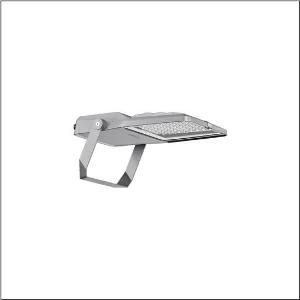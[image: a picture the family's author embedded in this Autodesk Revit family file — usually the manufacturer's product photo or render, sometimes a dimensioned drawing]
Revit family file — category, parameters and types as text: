
# Revit family: floodlight_fl_21_mini___pl33t_5xa7776b2f1a_8d7b
name_source: partatom
category: Lighting Fixtures
units: mm (PartAtom-declared; Revit-internal decimal feet)

## family parameters
Cut with Voids When Loaded = No
Host = Face
Light Source = No
Part Type = Normal
Room Calculation Point = No
Round Connector Dimension = Use Diameter
Shared = No

## types (1)
- --- (1 x LED, 6150 lm, 45.7 W, 3000K)
    Apparent Load = 46 VA
    CIE Flux Codes = 26 75 99 100 100
    Color Rendering = 70
    Color Temperature = 3000K
    Default Elevation = 1800 mm
    Description = Floodlight FL 21 mini, floodlight, primary light control with lens, of PMMA, primary optical cover: protective disc, of toughened safety glass, transparent, light distribution: PL33T, light emission: direct distribution, installation type: surface-mounted, LED, High Power LED, rated luminous flux: 6.150lm, luminous efficacy: 135lm/W, light colour: 730, colour temperature: 3000K, control: flexible luminous flux parameterisation, time-dependent luminous flux control, constant luminous flux control, overheat protection, presetting dimming logarithmic, with terminal, 6-pole, mains connection: 220..240V, AC, 50/60Hz, start of lifetime: 46W, end of service life: 48W, reduction: 22W, luminaire housing, of diecast aluminium, powder-coated, Siteco® metallic grey (DB 702S), corrosivity category C5 mid according to DIN EN ISO 12944, sealing non-destructively replaceable, mounting bracket, of steel, galvanised, powder-coated, Siteco® metallic grey (DB 702S), Smart Interface below and above, protection rating (complete): IP66, insulation class (complete): insulation class II (safety insulation), certification: CE, ENEC, VDE, protection symbol: D, impact resistance: IK08, permissible operating ambient temperature: -40..+40°C, permissible operating ambient temperature for outdoor applications: -40..+50°C, standard: DIN EN 12944, LABS conformity tested according to VDMA 24364:2018-05, packaging unit: 1 piece

Light Distribution: PL33T
    Height = 70 mm
    Lamp = 1 x LED
    Lamp Light Flux = 6150 lm
    Lamp Power = 45.7 W
    Lamp count = 1
    Length = 485 mm
    Luminous efficacy = 135 lm/W
    Manufacturer = Siteco
    ModVariant = No
    Model = 5XA7776B2F1A
    Number of Poles = 1
    OnlyDefault = Yes
    Power Factor = 1
    Product Name = Floodlight FL 21 mini | PL33T
    Product group = floodlight | pylon annexe
    ProductGroupID = 6200
    Protection Class = Protection class II
    Protection Degree = IP 66
    RLX_Detail_Level = 1
    RLX_Emergency_Light_Flux = 0 lm
    RLX_Emergency_Type = 0
    RLX_Emergency_Type_DB = No
    RlxData = <blob elided: 95769 chars, md5=1dcbc59d>
    Socket = socket
    Standby Power = 0 W
    System Light Flux = 6150 lm
    System Power = 46 W
    Type Comments = factory setting: luminous flux: 100 % | dim-lin: 254 | 463 mA
    Type Image = l_1006845.jpg
    URL = http://relux.com
    VarID = @adj_081123
    Voltage = 0 V
    Weight = 0.00 kg
    Width = 337 mm

## geometry (parser evidence)
native form markers: Blend x4, Sweep x13
no freeform markers — native parametric forms only
